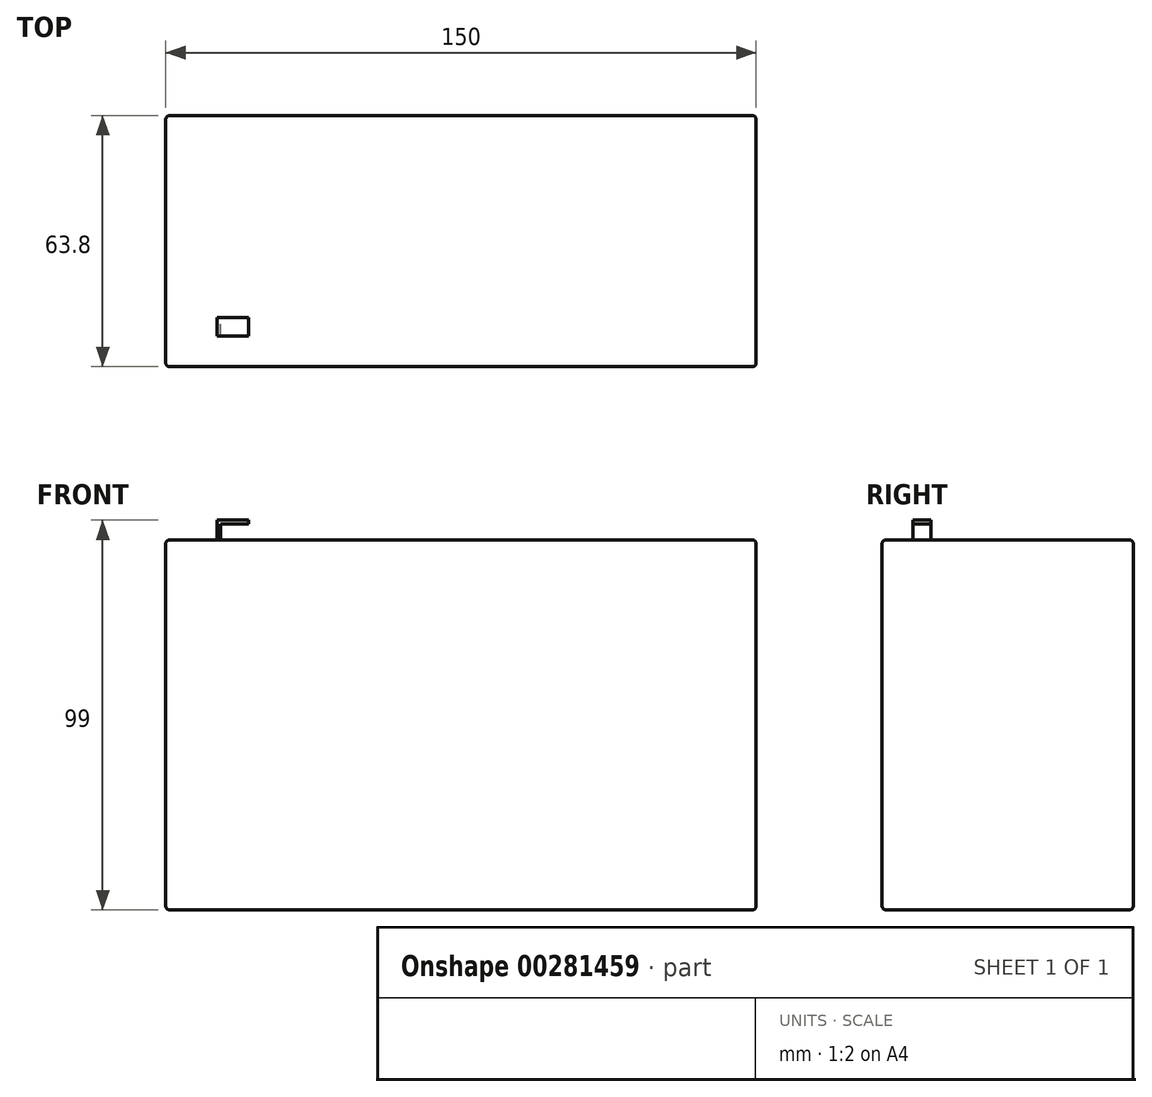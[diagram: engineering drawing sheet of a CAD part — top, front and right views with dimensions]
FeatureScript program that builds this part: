
annotation { "Feature Type Name" : "Feature", "Feature Type Description" : "" }
export const myFeature = defineFeature(function(context is Context, id is Id, definition is map)
    precondition{}
    {
        {
            var Q0;
            Q0=qCreatedBy(makeId("Top.planeOp"),FACE);
            var sketch = newSketch(context, id + "F0", { "sketchPlane" : qUnion([Q0])});
            skLineSegment(sketch, "E0.bottom", {"start": v(-75, 31.9) * mm, "end": v(75, 31.9) * mm});
            skLineSegment(sketch, "E0.top", {"start": v(-75, -31.9) * mm, "end": v(75, -31.9) * mm});
            skLineSegment(sketch, "E0.left", {"start": v(-75, 31.9) * mm, "end": v(-75, -31.9) * mm});
            skLineSegment(sketch, "E0.right", {"start": v(75, 31.9) * mm, "end": v(75, -31.9) * mm});
            skPoint(sketch, "E0.middle", {"position": v(0, 0) * mm});
            skSolve(sketch);
        }
        {
            var Q0;
            Q0=makeQuery(id+"F0.imprint","IMPRINT",FACE,{"disambiguationData":[TD([[makeQuery(id+"F0.imprint","IMPRINT",EDGE,{"derivedFrom":sQuery(id+"F0.wireOp",EDGE,"E0.bottom")}),-1.0]])]});
            extrude(context, id + "F1", {"entities" : qUnion([Q0]), "depth" : 94 * mm});
        }
        {
            var Q0;
            Q0=qCreatedBy(makeId("Front.planeOp"),FACE);
            cPlane(context, id + "F2", {"entities" : qUnion([Q0]), "cplaneType" : CPlaneType.OFFSET, "offset" : 21.75 * mm, "width" : 152.4 * mm, "height" : 152.4 * mm});
        }
        {
            var Q0;
            Q0=qCreatedBy(id+"F2.planeOp",FACE);
            var sketch = newSketch(context, id + "F3", { "sketchPlane" : qUnion([Q0])});
            skLineSegment(sketch, "E1", {"start": v(-62, 94) * mm, "end": v(-62, 99) * mm});
            skLineSegment(sketch, "E2", {"start": v(-62, 99) * mm, "end": v(-54, 99) * mm});
            skLineSegment(sketch, "E3", {"start": v(-54, 99) * mm, "end": v(-54, 98) * mm});
            skLineSegment(sketch, "E4", {"start": v(-54, 98) * mm, "end": v(-61, 98) * mm});
            skLineSegment(sketch, "E5", {"start": v(-61, 98) * mm, "end": v(-61, 94) * mm});
            skLineSegment(sketch, "E6", {"start": v(-61, 94) * mm, "end": v(-62, 94) * mm});
            skSolve(sketch);
        }
        {
            var Q0;
            Q0=makeQuery(id+"F3.imprint","IMPRINT",FACE,{"disambiguationData":[TD([[makeQuery(id+"F3.imprint","IMPRINT",EDGE,{"derivedFrom":sQuery(id+"F3.wireOp",EDGE,"E1")}),-1.0]])]});
            extrude(context, id + "F4", {"entities" : qUnion([Q0]), "operationType" : NewBodyOperationType.ADD, "endBound" : BoundingType.SYMMETRIC, "depth" : 4.6 * mm});
        }
        {
            var Q0;
            Q0=makeQuery(id+"F1.opExtrude","CAP_EDGE",EDGE,{"disambiguationData":[OSD([sQuery(id+"F0.wireOp",EDGE,"E0.top")])],"isStart":false});
            var Q1;
            Q1=makeQuery(id+"F1.opExtrude","CAP_EDGE",EDGE,{"disambiguationData":[OSD([sQuery(id+"F0.wireOp",EDGE,"E0.right")])],"isStart":false});
            var Q2;
            Q2=makeQuery(id+"F1.opExtrude","CAP_EDGE",EDGE,{"disambiguationData":[OSD([sQuery(id+"F0.wireOp",EDGE,"E0.bottom")])],"isStart":false});
            var Q3;
            Q3=makeQuery(id+"F1.opExtrude","CAP_EDGE",EDGE,{"disambiguationData":[OSD([sQuery(id+"F0.wireOp",EDGE,"E0.left")])],"isStart":false});
            var Q4;
            Q4=makeQuery(id+"F1.opExtrude","SWEPT_FACE",FACE,{"disambiguationData":[OSD([sQuery(id+"F0.wireOp",EDGE,"E0.top")])]});
            var Q5;
            Q5=makeQuery(id+"F1.opExtrude","SWEPT_FACE",FACE,{"disambiguationData":[OSD([sQuery(id+"F0.wireOp",EDGE,"E0.right")])]});
            var Q6;
            Q6=makeQuery(id+"F1.opExtrude","SWEPT_FACE",FACE,{"disambiguationData":[OSD([sQuery(id+"F0.wireOp",EDGE,"E0.bottom")])]});
            var Q7;
            Q7=makeQuery(id+"F1.opExtrude","CAP_FACE",FACE,{"disambiguationData":[OSD([sQuery(id+"F0.wireOp",EDGE,"E0.bottom"),sQuery(id+"F0.wireOp",EDGE,"E0.top"),sQuery(id+"F0.wireOp",EDGE,"E0.left"),sQuery(id+"F0.wireOp",EDGE,"E0.right")])],"isStart":true});
            var Q8;
            Q8=makeQuery(id+"F1.opExtrude","SWEPT_FACE",FACE,{"disambiguationData":[OSD([sQuery(id+"F0.wireOp",EDGE,"E0.left")])]});
            fillet(context, id + "F5", {"entities" : qUnion([Q0, Q1, Q2, Q3, Q4, Q5, Q6, Q7, Q8]), "radius" : 1 * mm, "tangentPropagation" : true, "allowEdgeOverflow" : false});
        }
    });
